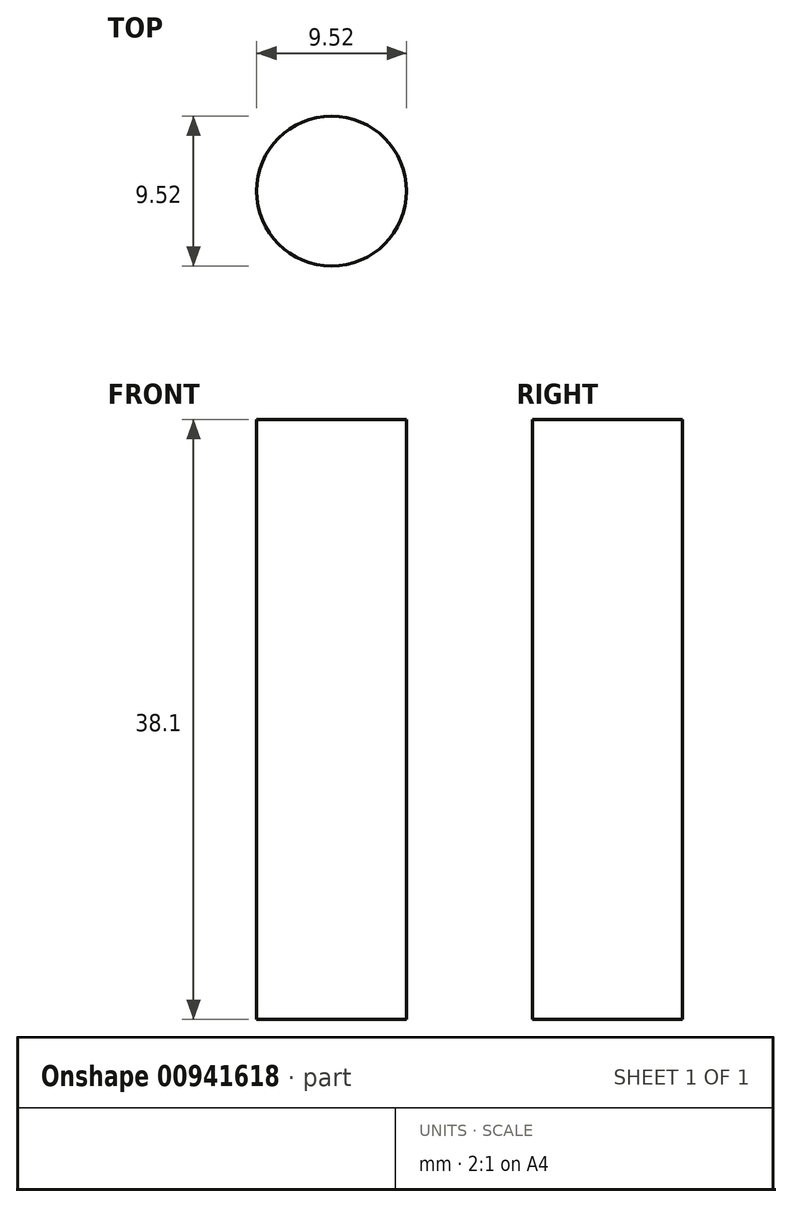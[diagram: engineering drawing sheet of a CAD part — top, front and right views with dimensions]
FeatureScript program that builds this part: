
annotation { "Feature Type Name" : "Feature", "Feature Type Description" : "" }
export const myFeature = defineFeature(function(context is Context, id is Id, definition is map)
    precondition{}
    {
        {
            var Q0;
            Q0=qCreatedBy(makeId("Top.planeOp"),FACE);
            var sketch = newSketch(context, id + "F0", { "sketchPlane" : qUnion([Q0])});
            skCircle(sketch, "E0", {"center": v(0, 0) * mm, "radius": 4.76 * mm});
            skSolve(sketch);
        }
        {
            var Q0;
            Q0=makeQuery(id+"F0.imprint","IMPRINT",FACE,{"disambiguationData":[TD([[makeQuery(id+"F0.imprint","IMPRINT",EDGE,{"derivedFrom":sQuery(id+"F0.wireOp",EDGE,"E0")}),1.0]])]});
            extrude(context, id + "F1", {"entities" : qUnion([Q0]), "endBound" : BoundingType.SYMMETRIC, "depth" : 38.1 * mm, "offsetDistance" : 25.4 * mm});
        }
    });
